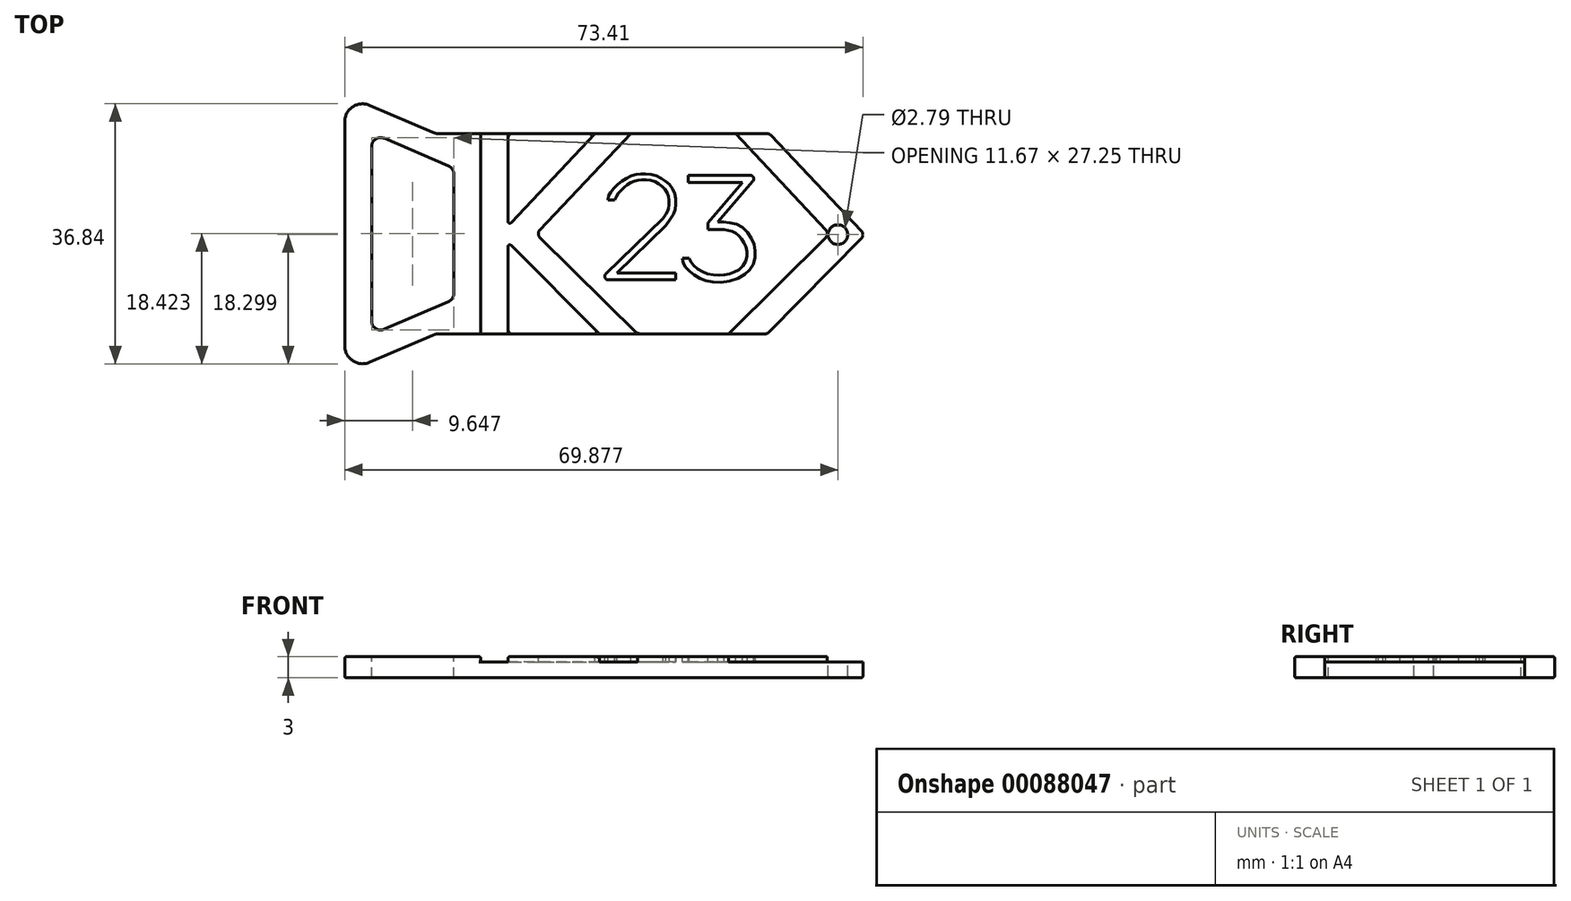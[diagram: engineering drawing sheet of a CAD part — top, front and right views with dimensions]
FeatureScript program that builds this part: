
annotation { "Feature Type Name" : "Feature", "Feature Type Description" : "" }
export const myFeature = defineFeature(function(context is Context, id is Id, definition is map)
    precondition{}
    {
        {
            var Q0;
            Q0=qCreatedBy(makeId("Top.planeOp"),FACE);
            var sketch = newSketch(context, id + "F0", { "sketchPlane" : qUnion([Q0])});
            skLineSegment(sketch, "E0", {"start": v(-56.05, -53.7) * mm, "end": v(-56.05, -52.7) * mm});
            skLineSegment(sketch, "E1", {"start": v(-56.05, -53.7) * mm, "end": v(-65.6, -53.7) * mm});
            skLineSegment(sketch, "E2", {"start": v(-65.96, -52.83) * mm, "end": v(-57.87, -44.95) * mm});
            skLineSegment(sketch, "E3", {"start": v(-56.05, -52.7) * mm, "end": v(-64.4, -52.7) * mm});
            skLineSegment(sketch, "E4", {"start": v(-64.4, -52.7) * mm, "end": v(-65.1, -52) * mm, "construction": true});
            skLineSegment(sketch, "E5", {"start": v(-64.4, -52.7) * mm, "end": v(-57.5, -45.98) * mm});
            skFitSpline(sketch, "E6", {"points": [v(-57.87, -44.95) * mm, v(-57.21, -43.95) * mm, v(-57.07, -43.34) * mm, v(-57.04, -42.12) * mm, v(-57.36, -41.17) * mm, v(-58.14, -40.3) * mm, v(-59.25, -39.7) * mm, v(-60.57, -39.5) * mm, v(-61.62, -39.61) * mm, v(-62.56, -40) * mm, v(-63.57, -40.77) * mm, v(-64.27, -41.53) * mm, v(-64.68, -42.35) * mm], "startDerivative": vector(12.76, 14.3) * mm, "endDerivative": vector(-4.73, -10.96) * mm});
            skLineSegment(sketch, "E7", {"start": v(-64.68, -42.35) * mm, "end": v(-65.68, -42.35) * mm});
            skFitSpline(sketch, "E8", {"points": [v(-65.68, -42.35) * mm, v(-65.54, -41.73) * mm, v(-65.05, -41) * mm, v(-64.16, -40.06) * mm, v(-63.3, -39.44) * mm, v(-62.23, -38.9) * mm, v(-61.22, -38.7) * mm, v(-60.27, -38.67) * mm, v(-59.04, -38.87) * mm, v(-57.9, -39.43) * mm, v(-57.12, -40.02) * mm, v(-56.37, -40.99) * mm, v(-56.08, -42.15) * mm, v(-56.1, -43.36) * mm, v(-56.4, -44.4) * mm, v(-57.5, -45.98) * mm], "startDerivative": vector(1.92, 12.36) * mm, "endDerivative": vector(-15.52, -18.51) * mm});
            skLineSegment(sketch, "E9", {"start": v(-54.29, -38.89) * mm, "end": v(-54.29, -39.89) * mm});
            skLineSegment(sketch, "E10", {"start": v(-54.29, -38.89) * mm, "end": v(-45.5, -38.89) * mm});
            skLineSegment(sketch, "E11", {"start": v(-45.12, -39.73) * mm, "end": v(-50.08, -45.46) * mm});
            skLineSegment(sketch, "E12", {"start": v(-54.29, -39.89) * mm, "end": v(-46.58, -39.89) * mm});
            skLineSegment(sketch, "E13", {"start": v(-46.58, -39.89) * mm, "end": v(-45.82, -40.54) * mm});
            skLineSegment(sketch, "E14", {"start": v(-46.58, -39.89) * mm, "end": v(-51.5, -45.58) * mm});
            skLineSegment(sketch, "E15", {"start": v(-51.5, -45.58) * mm, "end": v(-51.5, -46.58) * mm});
            skPoint(sketch, "E16.visualSharp", {"position": v(-44.39, -38.89) * mm});
            skArc(sketch, "E16.filletArc", {"start": v(-45.12, -39.73) * mm, "mid": v(-45.04, -39.18) * mm, "end": v(-45.5, -38.89) * mm});
            skPoint(sketch, "E17.visualSharp", {"position": v(-66.86, -53.7) * mm});
            skArc(sketch, "E17.filletArc", {"start": v(-65.96, -52.83) * mm, "mid": v(-66.08, -53.39) * mm, "end": v(-65.6, -53.7) * mm});
            skLineSegment(sketch, "E18", {"start": v(-51.5, -46.58) * mm, "end": v(-49.18, -46.58) * mm});
            skFitSpline(sketch, "E19", {"points": [v(-49.18, -46.58) * mm, v(-48.4, -46.73) * mm, v(-47.53, -47.1) * mm, v(-46.88, -47.72) * mm, v(-46.37, -48.48) * mm, v(-45.96, -49.59) * mm, v(-46.08, -50.86) * mm, v(-46.91, -52.1) * mm, v(-48.2, -52.78) * mm, v(-49.41, -53.02) * mm, v(-51.2, -52.93) * mm, v(-52.71, -52.31) * mm, v(-53.8, -51.36) * mm, v(-54.14, -50.65) * mm], "startDerivative": vector(12.2, -1.75) * mm, "endDerivative": vector(-3.87, 14.26) * mm});
            skLineSegment(sketch, "E20", {"start": v(-54.14, -50.65) * mm, "end": v(-55.14, -50.65) * mm});
            skFitSpline(sketch, "E21", {"points": [v(-55.14, -50.65) * mm, v(-54.93, -51.46) * mm, v(-54.52, -52.07) * mm, v(-53.73, -52.79) * mm, v(-52.54, -53.54) * mm, v(-51.15, -53.96) * mm, v(-48.91, -53.95) * mm, v(-46.67, -53.17) * mm, v(-45.5, -52.15) * mm, v(-44.89, -50.8) * mm, v(-44.85, -49.23) * mm, v(-45.25, -47.96) * mm, v(-46.29, -46.5) * mm, v(-47.53, -45.8) * mm, v(-49.08, -45.5) * mm, v(-50.08, -45.46) * mm], "startDerivative": vector(0.7, -15.69) * mm, "endDerivative": vector(-16.7, -0.1) * mm});
            skLineSegment(sketch, "E22", {"start": v(-42.77, -33) * mm, "end": v(-29.26, -47.3) * mm});
            skLineSegment(sketch, "E23", {"start": v(-29.26, -47.3) * mm, "end": v(-43.06, -61.34) * mm});
            skLineSegment(sketch, "E24", {"start": v(-43.06, -61.34) * mm, "end": v(-48.57, -61.34) * mm});
            skLineSegment(sketch, "E25", {"start": v(-83.67, -61.34) * mm, "end": v(-83.67, -33) * mm});
            skLineSegment(sketch, "E26", {"start": v(-79.82, -33) * mm, "end": v(-79.82, -45.42) * mm});
            skLineSegment(sketch, "E27", {"start": v(-66.89, -61.34) * mm, "end": v(-79.4, -48.8) * mm});
            skLineSegment(sketch, "E28", {"start": v(-61.48, -61.34) * mm, "end": v(-75.82, -47.2) * mm});
            skLineSegment(sketch, "E29", {"start": v(-75.82, -47.2) * mm, "end": v(-62.44, -33) * mm});
            skLineSegment(sketch, "E30", {"start": v(-79.39, -45.59) * mm, "end": v(-67.52, -33) * mm});
            skLineSegment(sketch, "E31", {"start": v(-48.57, -61.34) * mm, "end": v(-34.3, -47.17) * mm});
            skLineSegment(sketch, "E32", {"start": v(-34.3, -47.17) * mm, "end": v(-47.59, -33) * mm});
            skLineSegment(sketch, "E33.trimOffspring", {"start": v(-47.59, -33) * mm, "end": v(-42.77, -33) * mm});
            skLineSegment(sketch, "E34.trimOffspring", {"start": v(-67.52, -33) * mm, "end": v(-62.44, -33) * mm});
            skLineSegment(sketch, "E35.trimOffspring", {"start": v(-79.82, -48.98) * mm, "end": v(-79.82, -61.34) * mm});
            skLineSegment(sketch, "E36.trimOffspring", {"start": v(-79.82, -61.34) * mm, "end": v(-83.67, -61.34) * mm});
            skLineSegment(sketch, "E37.trimOffspring", {"start": v(-61.48, -61.34) * mm, "end": v(-66.89, -61.34) * mm});
            skLineSegment(sketch, "E38", {"start": v(-29.26, -61.34) * mm, "end": v(-29.26, -33) * mm, "construction": true});
            skLineSegment(sketch, "E39", {"start": v(-29.26, -33) * mm, "end": v(-83.67, -33) * mm, "construction": true});
            skLineSegment(sketch, "E40", {"start": v(-79.82, -33) * mm, "end": v(-83.67, -33) * mm});
            skLineSegment(sketch, "E41", {"start": v(-83.67, -33) * mm, "end": v(-83.67, -61.34) * mm, "construction": true});
            skLineSegment(sketch, "E42", {"start": v(-29.26, -61.34) * mm, "end": v(-83.67, -61.34) * mm, "construction": true});
            skLineSegment(sketch, "E43", {"start": v(-29.26, -47.17) * mm, "end": v(-26.78, -47.17) * mm, "construction": true});
            skLineSegment(sketch, "E44", {"start": v(-56.46, -28.75) * mm, "end": v(-56.46, -33) * mm, "construction": true});
            skLineSegment(sketch, "E45", {"start": v(-29.26, -47.17) * mm, "end": v(-83.67, -47.17) * mm, "construction": true});
            skLineSegment(sketch, "E46", {"start": v(-56.46, -33) * mm, "end": v(-56.46, -47.17) * mm, "construction": true});
            skPoint(sketch, "E47.visualSharp", {"position": v(-79.82, -46.06) * mm});
            skArc(sketch, "E47.filletArc", {"start": v(-79.82, -45.42) * mm, "mid": v(-79.66, -45.65) * mm, "end": v(-79.39, -45.59) * mm});
            skPoint(sketch, "E48.visualSharp", {"position": v(-79.82, -48.37) * mm});
            skArc(sketch, "E48.filletArc", {"start": v(-79.4, -48.8) * mm, "mid": v(-79.67, -48.75) * mm, "end": v(-79.82, -48.98) * mm});
            skLineSegment(sketch, "E49", {"start": v(-87.48, -55.6) * mm, "end": v(-87.48, -38.73) * mm});
            skLineSegment(sketch, "E50", {"start": v(-88.25, -37.57) * mm, "end": v(-97.37, -33.64) * mm});
            skLineSegment(sketch, "E51", {"start": v(-88.25, -56.77) * mm, "end": v(-97.37, -60.7) * mm});
            skLineSegment(sketch, "E52", {"start": v(-87.48, -47.17) * mm, "end": v(-93.25, -47.17) * mm, "construction": true});
            skLineSegment(sketch, "E53", {"start": v(-99.15, -34.8) * mm, "end": v(-99.15, -59.53) * mm});
            skPoint(sketch, "E54.visualSharp", {"position": v(-99.15, -32.88) * mm});
            skArc(sketch, "E54.filletArc", {"start": v(-97.37, -33.64) * mm, "mid": v(-98.57, -33.75) * mm, "end": v(-99.15, -34.8) * mm});
            skPoint(sketch, "E55.visualSharp", {"position": v(-99.15, -61.45) * mm});
            skArc(sketch, "E55.filletArc", {"start": v(-99.15, -59.53) * mm, "mid": v(-98.57, -60.59) * mm, "end": v(-97.37, -60.7) * mm});
            skPoint(sketch, "E56.visualSharp", {"position": v(-87.48, -37.9) * mm});
            skArc(sketch, "E56.filletArc", {"start": v(-87.48, -38.73) * mm, "mid": v(-87.69, -38.03) * mm, "end": v(-88.25, -37.57) * mm});
            skPoint(sketch, "E57.visualSharp", {"position": v(-87.48, -56.44) * mm});
            skArc(sketch, "E57.filletArc", {"start": v(-88.25, -56.77) * mm, "mid": v(-87.69, -56.3) * mm, "end": v(-87.48, -55.6) * mm});
            skLineSegment(sketch, "E58", {"start": v(-83.67, -33) * mm, "end": v(-42.77, -33) * mm});
            skLineSegment(sketch, "E59", {"start": v(-43.06, -61.34) * mm, "end": v(-83.67, -61.34) * mm});
            skLineSegment(sketch, "E60", {"start": v(-83.67, -33) * mm, "end": v(-89.5, -33) * mm});
            skLineSegment(sketch, "E61", {"start": v(-90.5, -32.79) * mm, "end": v(-99.41, -28.95) * mm});
            skLineSegment(sketch, "E62", {"start": v(-102.96, -31.29) * mm, "end": v(-102.96, -63.05) * mm});
            skLineSegment(sketch, "E63", {"start": v(-99.41, -65.38) * mm, "end": v(-90.5, -61.55) * mm});
            skLineSegment(sketch, "E64", {"start": v(-89.5, -61.34) * mm, "end": v(-83.67, -61.34) * mm});
            skPoint(sketch, "E65.visualSharp", {"position": v(-102.96, -27.43) * mm});
            skArc(sketch, "E65.filletArc", {"start": v(-99.41, -28.95) * mm, "mid": v(-101.81, -29.17) * mm, "end": v(-102.96, -31.29) * mm});
            skPoint(sketch, "E66.visualSharp", {"position": v(-102.96, -66.9) * mm});
            skArc(sketch, "E66.filletArc", {"start": v(-102.96, -63.05) * mm, "mid": v(-101.81, -65.17) * mm, "end": v(-99.41, -65.38) * mm});
            skPoint(sketch, "E67.visualSharp", {"position": v(-90.02, -61.34) * mm});
            skArc(sketch, "E67.filletArc", {"start": v(-89.5, -61.34) * mm, "mid": v(-90, -61.4) * mm, "end": v(-90.5, -61.55) * mm});
            skPoint(sketch, "E68.visualSharp", {"position": v(-90.02, -33) * mm});
            skArc(sketch, "E68.filletArc", {"start": v(-90.5, -32.79) * mm, "mid": v(-90, -32.94) * mm, "end": v(-89.5, -33) * mm});
            skSolve(sketch);
        }
        {
            var Q0;
            Q0=makeQuery(id+"F0.imprint","IMPRINT",FACE,{"disambiguationData":[TD([[makeQuery(id+"F0.imprint","IMPRINT",EDGE,{"derivedFrom":sQuery(id+"F0.wireOp",EDGE,"E25")}),1.0]])]});
            var Q1;
            {var subQ1=sQuery(id+"F0.wireOp",EDGE,"E25");Q1=makeQuery(id+"F0.imprint","IMPRINT",FACE,{"disambiguationData":[TD([[makeQuery(id+"F0.imprint","IMPRINT",EDGE,{"derivedFrom":subQ1}),-1.0]])]});}
            var Q2;
            {var subQ0=sQuery(id+"F0.wireOp",EDGE,"E26");Q2=makeQuery(id+"F0.imprint","IMPRINT",FACE,{"disambiguationData":[TD([[makeQuery(id+"F0.imprint","IMPRINT",EDGE,{"derivedFrom":subQ0}),1.0]])]});}
            var Q3;
            Q3=makeQuery(id+"F0.imprint","IMPRINT",FACE,{"disambiguationData":[TD([[makeQuery(id+"F0.imprint","IMPRINT",EDGE,{"derivedFrom":sQuery(id+"F0.wireOp",EDGE,"E0")}),-1.0]])]});
            var Q4;
            {var subQ4=sQuery(id+"F0.wireOp",EDGE,"E22");Q4=makeQuery(id+"F0.imprint","IMPRINT",FACE,{"disambiguationData":[TD([[makeQuery(id+"F0.imprint","IMPRINT",EDGE,{"derivedFrom":subQ4}),-1.0]])]});}
            var Q5;
            Q5=makeQuery(id+"F0.imprint","IMPRINT",FACE,{"disambiguationData":[TD([[makeQuery(id+"F0.imprint","IMPRINT",EDGE,{"derivedFrom":sQuery(id+"F0.wireOp",EDGE,"E9")}),1.0]])]});
            var Q6;
            Q6=makeQuery(id+"F0.imprint","IMPRINT",FACE,{"disambiguationData":[TD([[makeQuery(id+"F0.imprint","IMPRINT",EDGE,{"derivedFrom":sQuery(id+"F0.wireOp",EDGE,"E0")}),1.0]])]});
            var Q7;
            {var subQ0=sQuery(id+"F0.wireOp",EDGE,"E13");Q7=makeQuery(id+"F0.imprint","IMPRINT",FACE,{"disambiguationData":[TD([[makeQuery(id+"F0.imprint","IMPRINT",EDGE,{"derivedFrom":subQ0}),-1.0]])]});}
            var Q8;
            {var subQ0=sQuery(id+"F0.wireOp",EDGE,"E27");Q8=makeQuery(id+"F0.imprint","IMPRINT",FACE,{"disambiguationData":[TD([[makeQuery(id+"F0.imprint","IMPRINT",EDGE,{"derivedFrom":subQ0}),1.0]])]});}
            extrude(context, id + "F1", {"entities" : qUnion([Q0, Q1, Q2, Q3, Q4, Q5, Q6, Q7, Q8]), "oppositeDirection" : true, "depth" : 3 * mm});
        }
        {
            var Q0;
            {var subQ1=sQuery(id+"F0.wireOp",EDGE,"E25");Q0=makeQuery(id+"F0.imprint","IMPRINT",FACE,{"disambiguationData":[TD([[makeQuery(id+"F0.imprint","IMPRINT",EDGE,{"derivedFrom":subQ1}),-1.0]])]});}
            var Q1;
            {var subQ4=sQuery(id+"F0.wireOp",EDGE,"E22");Q1=makeQuery(id+"F0.imprint","IMPRINT",FACE,{"disambiguationData":[TD([[makeQuery(id+"F0.imprint","IMPRINT",EDGE,{"derivedFrom":subQ4}),-1.0]])]});}
            var Q2;
            Q2=makeQuery(id+"F0.imprint","IMPRINT",FACE,{"disambiguationData":[TD([[makeQuery(id+"F0.imprint","IMPRINT",EDGE,{"derivedFrom":sQuery(id+"F0.wireOp",EDGE,"E0")}),1.0]])]});
            var Q3;
            {var subQ0=sQuery(id+"F0.wireOp",EDGE,"E13");Q3=makeQuery(id+"F0.imprint","IMPRINT",FACE,{"disambiguationData":[TD([[makeQuery(id+"F0.imprint","IMPRINT",EDGE,{"derivedFrom":subQ0}),-1.0]])]});}
            var Q4;
            Q4=makeQuery(id+"F0.imprint","IMPRINT",FACE,{"disambiguationData":[TD([[makeQuery(id+"F0.imprint","IMPRINT",EDGE,{"derivedFrom":sQuery(id+"F0.wireOp",EDGE,"E9")}),1.0]])]});
            extrude(context, id + "F2", {"entities" : qUnion([Q0, Q1, Q2, Q3, Q4]), "operationType" : NewBodyOperationType.REMOVE, "oppositeDirection" : true, "depth" : .75 * mm});
        }
        {
            var Q0;
            Q0=makeQuery(id+"F1.opExtrude","SWEPT_EDGE",EDGE,{"disambiguationData":[OSD([sQuery(id+"F0.wireOp",EDGE,"E22"),sQuery(id+"F0.wireOp",EDGE,"E23")])]});
            var Q1;
            Q1=makeQuery(id+"F1.opExtrude","SWEPT_EDGE",EDGE,{"disambiguationData":[OSD([sQuery(id+"F0.wireOp",EDGE,"E23"),sQuery(id+"F0.wireOp",EDGE,"E59")])]});
            var Q2;
            Q2=makeQuery(id+"F1.opExtrude","SWEPT_EDGE",EDGE,{"disambiguationData":[OSD([sQuery(id+"F0.wireOp",EDGE,"E22"),sQuery(id+"F0.wireOp",EDGE,"E58")])]});
            fillet(context, id + "F3", {"entities" : qUnion([Q0, Q1, Q2]), "radius" : 0.76 * mm, "tangentPropagation" : true, "allowEdgeOverflow" : false});
        }
        {
            var Q0;
            Q0=makeQuery(id+"F2.boolean.opBoolean","COPY",EDGE,{"derivedFrom":makeQuery(id+"F2.opExtrude","SWEPT_EDGE",EDGE,{"disambiguationData":[OSD([sQuery(id+"F0.wireOp",EDGE,"E31"),sQuery(id+"F0.wireOp",EDGE,"E32")])]})});
            var Q1;
            Q1=makeQuery(id+"F2.boolean.opBoolean","COPY",EDGE,{"derivedFrom":makeQuery(id+"F2.opExtrude","SWEPT_EDGE",EDGE,{"disambiguationData":[OSD([sQuery(id+"F0.wireOp",EDGE,"E31"),sQuery(id+"F0.wireOp",EDGE,"E59")])]})});
            var Q2;
            Q2=makeQuery(id+"F2.boolean.opBoolean","COPY",EDGE,{"derivedFrom":makeQuery(id+"F2.opExtrude","SWEPT_EDGE",EDGE,{"disambiguationData":[OSD([sQuery(id+"F0.wireOp",EDGE,"E32"),sQuery(id+"F0.wireOp",EDGE,"E58")])]})});
            var Q3;
            Q3=makeQuery(id+"F2.boolean.opBoolean","COPY",EDGE,{"derivedFrom":makeQuery(id+"F2.opExtrude","SWEPT_EDGE",EDGE,{"disambiguationData":[OSD([sQuery(id+"F0.wireOp",EDGE,"E28"),sQuery(id+"F0.wireOp",EDGE,"E29")])]})});
            fillet(context, id + "F4", {"entities" : qUnion([Q0, Q1, Q2, Q3]), "radius" : 0.76 * mm, "tangentPropagation" : true, "allowEdgeOverflow" : false});
        }
        {
            var Q0;
            Q0=makeQuery(id+"F2.boolean.opBoolean","COPY",FACE,{"derivedFrom":makeQuery(id+"F2.opExtrude","CAP_FACE",FACE,{"disambiguationData":[OSD([sQuery(id+"F0.wireOp",EDGE,"E22"),sQuery(id+"F0.wireOp",EDGE,"E23"),sQuery(id+"F0.wireOp",EDGE,"E31"),sQuery(id+"F0.wireOp",EDGE,"E32"),sQuery(id+"F0.wireOp",EDGE,"E58"),sQuery(id+"F0.wireOp",EDGE,"E59")])],"isStart":false})});
            var sketch = newSketch(context, id + "F5", { "sketchPlane" : qUnion([Q0])});
            skCircle(sketch, "E69", {"center": v(-33.08, -47.3) * mm, "radius": 1.4 * mm});
            skLineSegment(sketch, "E70", {"start": v(-29.55, -47.3) * mm, "end": v(-34.6, -47.3) * mm, "construction": true});
            skPoint(sketch, "E70.startSnap0", {"position": v(-29.55, -47.3) * mm});
            skSolve(sketch);
        }
        {
            var Q0;
            Q0=makeQuery(id+"F5.imprint","IMPRINT",FACE,{"disambiguationData":[TD([[makeQuery(id+"F5.imprint","IMPRINT",EDGE,{"derivedFrom":sQuery(id+"F5.wireOp",EDGE,"E69")}),1.0]])]});
            extrude(context, id + "F6", {"entities" : qUnion([Q0]), "operationType" : NewBodyOperationType.REMOVE, "endBound" : BoundingType.THROUGH_ALL, "oppositeDirection" : true, "depth" : 25.4 * mm});
        }
        {
            var Q0;
            {var subQ0=sQuery(id+"F0.wireOp",EDGE,"E64");var subQ1=sQuery(id+"F0.wireOp",EDGE,"E59");Q0=makeQuery(id+"F2.boolean.opBoolean","SPLIT",FACE,{"disambiguationData":[TD([makeQuery(id+"F2.opExtrude","SWEPT_FACE",FACE,{"disambiguationData":[OSD([sQuery(id+"F0.wireOp",EDGE,"E27")])]})])],"derivedFrom":makeQuery(id+"F1.opExtrude","CAP_FACE",FACE,{"disambiguationData":[OSD([sQuery(id+"F0.wireOp",EDGE,"E22"),sQuery(id+"F0.wireOp",EDGE,"E23"),sQuery(id+"F0.wireOp",EDGE,"E49"),sQuery(id+"F0.wireOp",EDGE,"E50"),sQuery(id+"F0.wireOp",EDGE,"E51"),sQuery(id+"F0.wireOp",EDGE,"E53"),sQuery(id+"F0.wireOp",EDGE,"E54.filletArc"),sQuery(id+"F0.wireOp",EDGE,"E55.filletArc"),sQuery(id+"F0.wireOp",EDGE,"E56.filletArc"),sQuery(id+"F0.wireOp",EDGE,"E57.filletArc"),sQuery(id+"F0.wireOp",EDGE,"E58"),subQ1,sQuery(id+"F0.wireOp",EDGE,"E60"),sQuery(id+"F0.wireOp",EDGE,"E61"),sQuery(id+"F0.wireOp",EDGE,"E62"),sQuery(id+"F0.wireOp",EDGE,"E63"),subQ0,sQuery(id+"F0.wireOp",EDGE,"E65.filletArc"),sQuery(id+"F0.wireOp",EDGE,"E66.filletArc"),sQuery(id+"F0.wireOp",EDGE,"E67.filletArc"),sQuery(id+"F0.wireOp",EDGE,"E68.filletArc")])],"isStart":true})});}
            var Q1;
            Q1=makeQuery(id+"F2.boolean.opBoolean","COPY",EDGE,{"derivedFrom":makeQuery(id+"F2.opExtrude","CAP_EDGE",EDGE,{"disambiguationData":[OSD([sQuery(id+"F0.wireOp",EDGE,"E25")])],"isStart":true})});
            var Q2;
            {var subQ0=sQuery(id+"F0.wireOp",EDGE,"E60");var subQ1=sQuery(id+"F0.wireOp",EDGE,"E58");Q2=makeQuery(id+"F2.boolean.opBoolean","SPLIT",FACE,{"disambiguationData":[TD([makeQuery(id+"F2.opExtrude","SWEPT_FACE",FACE,{"disambiguationData":[OSD([sQuery(id+"F0.wireOp",EDGE,"E26")])]})])],"derivedFrom":makeQuery(id+"F1.opExtrude","CAP_FACE",FACE,{"disambiguationData":[OSD([sQuery(id+"F0.wireOp",EDGE,"E22"),sQuery(id+"F0.wireOp",EDGE,"E23"),sQuery(id+"F0.wireOp",EDGE,"E49"),sQuery(id+"F0.wireOp",EDGE,"E50"),sQuery(id+"F0.wireOp",EDGE,"E51"),sQuery(id+"F0.wireOp",EDGE,"E53"),sQuery(id+"F0.wireOp",EDGE,"E54.filletArc"),sQuery(id+"F0.wireOp",EDGE,"E55.filletArc"),sQuery(id+"F0.wireOp",EDGE,"E56.filletArc"),sQuery(id+"F0.wireOp",EDGE,"E57.filletArc"),subQ1,sQuery(id+"F0.wireOp",EDGE,"E59"),subQ0,sQuery(id+"F0.wireOp",EDGE,"E61"),sQuery(id+"F0.wireOp",EDGE,"E62"),sQuery(id+"F0.wireOp",EDGE,"E63"),sQuery(id+"F0.wireOp",EDGE,"E64"),sQuery(id+"F0.wireOp",EDGE,"E65.filletArc"),sQuery(id+"F0.wireOp",EDGE,"E66.filletArc"),sQuery(id+"F0.wireOp",EDGE,"E67.filletArc"),sQuery(id+"F0.wireOp",EDGE,"E68.filletArc")])],"isStart":true})});}
            var Q3;
            {var subQ0=sQuery(id+"F0.wireOp",EDGE,"E64");var subQ1=sQuery(id+"F0.wireOp",EDGE,"E59");Q3=makeQuery(id+"F2.boolean.opBoolean","SPLIT",EDGE,{"disambiguationData":[TD([makeQuery(id+"F2.opExtrude","SWEPT_FACE",FACE,{"disambiguationData":[OSD([sQuery(id+"F0.wireOp",EDGE,"E28")])]})])],"derivedFrom":makeQuery(id+"F1.opExtrude","CAP_EDGE",EDGE,{"disambiguationData":[OSD([subQ1,subQ0])],"isStart":true})});}
            var Q4;
            Q4=makeQuery(id+"F2.boolean.opBoolean","COPY",EDGE,{"derivedFrom":makeQuery(id+"F2.opExtrude","CAP_EDGE",EDGE,{"disambiguationData":[OSD([sQuery(id+"F0.wireOp",EDGE,"E28")])],"isStart":true})});
            var Q5;
            {var subQ0=sQuery(id+"F0.wireOp",EDGE,"E59");Q5=makeQuery(id+"F2.boolean.opBoolean","COPY",EDGE,{"derivedFrom":makeQuery(id+"F2.opExtrude","CAP_EDGE",EDGE,{"disambiguationData":[OSD([subQ0]),TDD([makeQuery(id+"F0.imprint","IMPRINT",EDGE,{"disambiguationData":[TD([[makeQuery(id+"F0.imprint","INTERSECT",VERTEX,{"derivedFrom":[sQuery(id+"F0.wireOp",EDGE,"E27"),subQ0]}),1.0]])],"derivedFrom":subQ0})])],"isStart":false})});}
            var Q6;
            {var subQ0=sQuery(id+"F0.wireOp",EDGE,"E59");Q6=makeQuery(id+"F2.boolean.opBoolean","COPY",EDGE,{"derivedFrom":makeQuery(id+"F2.opExtrude","CAP_EDGE",EDGE,{"disambiguationData":[OSD([subQ0]),TDD([makeQuery(id+"F0.imprint","IMPRINT",EDGE,{"disambiguationData":[TD([[makeQuery(id+"F0.imprint","INTERSECT",VERTEX,{"derivedFrom":[sQuery(id+"F0.wireOp",EDGE,"E35.trimOffspring"),subQ0]}),-1.0]])],"derivedFrom":subQ0})])],"isStart":false})});}
            var Q7;
            Q7=makeQuery(id+"F2.boolean.opBoolean","COPY",EDGE,{"derivedFrom":makeQuery(id+"F2.opExtrude","SWEPT_EDGE",EDGE,{"disambiguationData":[OSD([sQuery(id+"F0.wireOp",EDGE,"E25"),sQuery(id+"F0.wireOp",EDGE,"E59"),sQuery(id+"F0.wireOp",EDGE,"E64")])]})});
            var Q8;
            Q8=makeQuery(id+"F2.boolean.opBoolean","COPY",EDGE,{"derivedFrom":makeQuery(id+"F2.opExtrude","SWEPT_EDGE",EDGE,{"disambiguationData":[OSD([sQuery(id+"F0.wireOp",EDGE,"E35.trimOffspring"),sQuery(id+"F0.wireOp",EDGE,"E59")])]})});
            var Q9;
            {var subQ0=sQuery(id+"F0.wireOp",EDGE,"E58");Q9=makeQuery(id+"F2.boolean.opBoolean","COPY",EDGE,{"derivedFrom":makeQuery(id+"F2.opExtrude","CAP_EDGE",EDGE,{"disambiguationData":[OSD([subQ0]),TDD([makeQuery(id+"F0.imprint","IMPRINT",EDGE,{"disambiguationData":[TD([[makeQuery(id+"F0.imprint","INTERSECT",VERTEX,{"derivedFrom":[sQuery(id+"F0.wireOp",EDGE,"E29"),subQ0]}),1.0]])],"derivedFrom":subQ0})])],"isStart":false})});}
            var Q10;
            Q10=makeQuery(id+"F2.boolean.opBoolean","COPY",EDGE,{"derivedFrom":makeQuery(id+"F2.opExtrude","SWEPT_EDGE",EDGE,{"disambiguationData":[OSD([sQuery(id+"F0.wireOp",EDGE,"E30"),sQuery(id+"F0.wireOp",EDGE,"E58")])]})});
            var Q11;
            Q11=makeQuery(id+"F2.boolean.opBoolean","COPY",EDGE,{"derivedFrom":makeQuery(id+"F2.opExtrude","SWEPT_EDGE",EDGE,{"disambiguationData":[OSD([sQuery(id+"F0.wireOp",EDGE,"E29"),sQuery(id+"F0.wireOp",EDGE,"E58")])]})});
            var Q12;
            {var subQ0=sQuery(id+"F0.wireOp",EDGE,"E58");Q12=makeQuery(id+"F2.boolean.opBoolean","COPY",EDGE,{"derivedFrom":makeQuery(id+"F2.opExtrude","CAP_EDGE",EDGE,{"disambiguationData":[OSD([subQ0]),TDD([makeQuery(id+"F0.imprint","IMPRINT",EDGE,{"disambiguationData":[TD([[makeQuery(id+"F0.imprint","INTERSECT",VERTEX,{"derivedFrom":[sQuery(id+"F0.wireOp",EDGE,"E26"),subQ0]}),1.0]])],"derivedFrom":subQ0})])],"isStart":false})});}
            var Q13;
            Q13=makeQuery(id+"F2.boolean.opBoolean","COPY",EDGE,{"derivedFrom":makeQuery(id+"F2.opExtrude","SWEPT_EDGE",EDGE,{"disambiguationData":[OSD([sQuery(id+"F0.wireOp",EDGE,"E25"),sQuery(id+"F0.wireOp",EDGE,"E58"),sQuery(id+"F0.wireOp",EDGE,"E60")])]})});
            var Q14;
            Q14=makeQuery(id+"F2.boolean.opBoolean","COPY",EDGE,{"derivedFrom":makeQuery(id+"F2.opExtrude","SWEPT_EDGE",EDGE,{"disambiguationData":[OSD([sQuery(id+"F0.wireOp",EDGE,"E26"),sQuery(id+"F0.wireOp",EDGE,"E58")])]})});
            var Q15;
            {var subQ0=sQuery(id+"F0.wireOp",EDGE,"E58");Q15=makeQuery(id+"F2.boolean.opBoolean","COPY",EDGE,{"derivedFrom":makeQuery(id+"F2.opExtrude","CAP_EDGE",EDGE,{"disambiguationData":[OSD([subQ0]),TDD([makeQuery(id+"F0.imprint","IMPRINT",EDGE,{"disambiguationData":[TD([[makeQuery(id+"F0.imprint","INTERSECT",VERTEX,{"derivedFrom":[sQuery(id+"F0.wireOp",EDGE,"E22"),subQ0]}),1.0]])],"derivedFrom":subQ0})])],"isStart":false})});}
            fillet(context, id + "F7", {"entities" : qUnion([Q0, Q1, Q2, Q3, Q4, Q5, Q6, Q7, Q8, Q9, Q10, Q11, Q12, Q13, Q14, Q15]), "radius" : 0.25 * mm, "tangentPropagation" : true, "allowEdgeOverflow" : false});
        }
        {
            var Q0;
            {var subQ0=sQuery(id+"F0.wireOp",EDGE,"E67.filletArc");var subQ1=sQuery(id+"F0.wireOp",EDGE,"E64");var subQ2=sQuery(id+"F0.wireOp",EDGE,"E59");Q0=makeQuery(id+"F2.boolean.opBoolean","SPLIT",EDGE,{"disambiguationData":[TD([makeQuery(id+"F1.opExtrude","SWEPT_FACE",FACE,{"disambiguationData":[OSD([subQ0])]})])],"derivedFrom":makeQuery(id+"F1.opExtrude","CAP_EDGE",EDGE,{"disambiguationData":[OSD([subQ2,subQ1])],"isStart":true})});}
            var Q1;
            Q1=makeQuery(id+"F1.opExtrude","CAP_EDGE",EDGE,{"disambiguationData":[OSD([sQuery(id+"F0.wireOp",EDGE,"E59"),sQuery(id+"F0.wireOp",EDGE,"E64")])],"isStart":false});
            var Q2;
            Q2=makeQuery(id+"F6.boolean.opBoolean","INTERSECT",EDGE,{"derivedFrom":[makeQuery(id+"F1.opExtrude","CAP_FACE",FACE,{"disambiguationData":[OSD([sQuery(id+"F0.wireOp",EDGE,"E22"),sQuery(id+"F0.wireOp",EDGE,"E23"),sQuery(id+"F0.wireOp",EDGE,"E49"),sQuery(id+"F0.wireOp",EDGE,"E50"),sQuery(id+"F0.wireOp",EDGE,"E51"),sQuery(id+"F0.wireOp",EDGE,"E53"),sQuery(id+"F0.wireOp",EDGE,"E54.filletArc"),sQuery(id+"F0.wireOp",EDGE,"E55.filletArc"),sQuery(id+"F0.wireOp",EDGE,"E56.filletArc"),sQuery(id+"F0.wireOp",EDGE,"E57.filletArc"),sQuery(id+"F0.wireOp",EDGE,"E58"),sQuery(id+"F0.wireOp",EDGE,"E59"),sQuery(id+"F0.wireOp",EDGE,"E60"),sQuery(id+"F0.wireOp",EDGE,"E61"),sQuery(id+"F0.wireOp",EDGE,"E62"),sQuery(id+"F0.wireOp",EDGE,"E63"),sQuery(id+"F0.wireOp",EDGE,"E64"),sQuery(id+"F0.wireOp",EDGE,"E65.filletArc"),sQuery(id+"F0.wireOp",EDGE,"E66.filletArc"),sQuery(id+"F0.wireOp",EDGE,"E67.filletArc"),sQuery(id+"F0.wireOp",EDGE,"E68.filletArc")])],"isStart":false}),makeQuery(id+"F6.opExtrude","SWEPT_FACE",FACE,{"disambiguationData":[OSD([sQuery(id+"F5.wireOp",EDGE,"E69")])]})]});
            var Q3;
            Q3=makeQuery(id+"F6.boolean.opBoolean","COPY",EDGE,{"derivedFrom":makeQuery(id+"F6.opExtrude","CAP_EDGE",EDGE,{"disambiguationData":[OSD([sQuery(id+"F5.wireOp",EDGE,"E69")])],"isStart":true})});
            fillet(context, id + "F8", {"entities" : qUnion([Q0, Q1, Q2, Q3]), "radius" : 0.25 * mm, "tangentPropagation" : true, "allowEdgeOverflow" : false});
        }
    });
